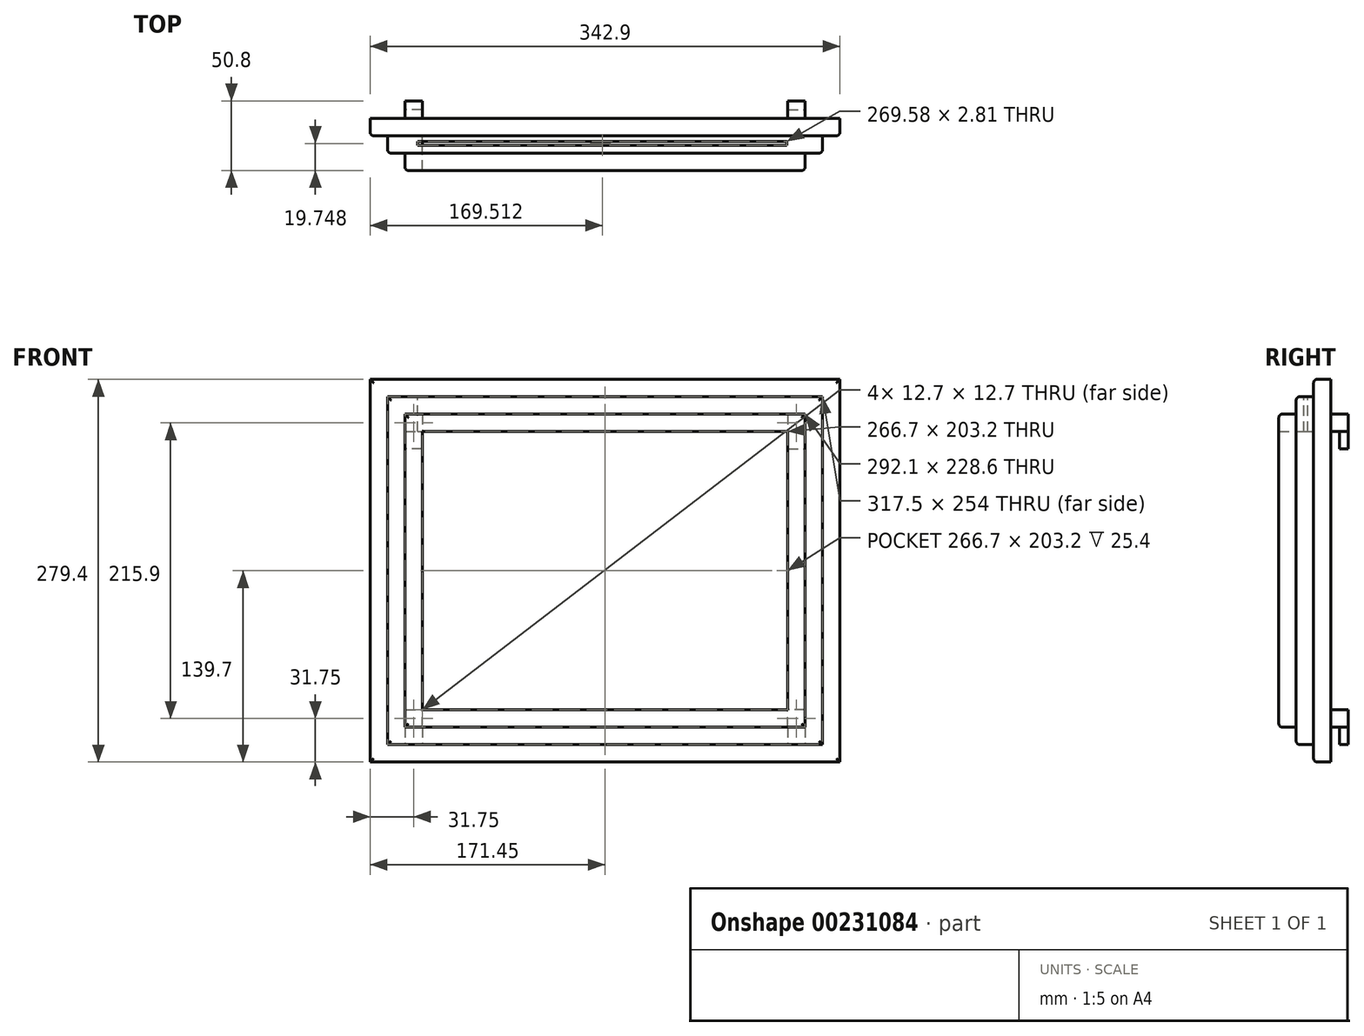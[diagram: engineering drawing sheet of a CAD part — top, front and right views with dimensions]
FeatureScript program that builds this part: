
annotation { "Feature Type Name" : "Feature", "Feature Type Description" : "" }
export const myFeature = defineFeature(function(context is Context, id is Id, definition is map)
    precondition{}
    {
        {
            var Q0;
            Q0=qCreatedBy(makeId("Front.planeOp"),FACE);
            var sketch = newSketch(context, id + "F0", { "sketchPlane" : qUnion([Q0])});
            skLineSegment(sketch, "E0.bottom", {"start": v(171.45, -139.7) * mm, "end": v(-171.45, -139.7) * mm});
            skLineSegment(sketch, "E0.top", {"start": v(171.45, 139.7) * mm, "end": v(-171.45, 139.7) * mm});
            skLineSegment(sketch, "E0.left", {"start": v(171.45, -139.7) * mm, "end": v(171.45, 139.7) * mm});
            skLineSegment(sketch, "E0.right", {"start": v(-171.45, -139.7) * mm, "end": v(-171.45, 139.7) * mm});
            skPoint(sketch, "E0.middle", {"position": v(0, 0) * mm});
            skSolve(sketch);
        }
        {
            var Q0;
            Q0 = qSketchRegion(id + "F0", true);
            extrude(context, id + "F1", {"entities" : qUnion([Q0]), "depth" : 12.7 * mm});
        }
        {
            var Q0;
            Q0=makeQuery(id+"F1.opExtrude","CAP_FACE",FACE,{"disambiguationData":[OSD([sQuery(id+"F0.wireOp",EDGE,"E0.bottom"),sQuery(id+"F0.wireOp",EDGE,"E0.top"),sQuery(id+"F0.wireOp",EDGE,"E0.left"),sQuery(id+"F0.wireOp",EDGE,"E0.right")])],"isStart":false});
            var sketch = newSketch(context, id + "F2", { "sketchPlane" : qUnion([Q0])});
            skLineSegment(sketch, "E1.bottom", {"start": v(158.75, 127) * mm, "end": v(-158.75, 127) * mm});
            skLineSegment(sketch, "E1.top", {"start": v(158.75, -127) * mm, "end": v(-158.75, -127) * mm});
            skLineSegment(sketch, "E1.left", {"start": v(158.75, 127) * mm, "end": v(158.75, -127) * mm});
            skLineSegment(sketch, "E1.right", {"start": v(-158.75, 127) * mm, "end": v(-158.75, -127) * mm});
            skPoint(sketch, "E1.middle", {"position": v(0, 0) * mm});
            skSolve(sketch);
        }
        {
            var Q0;
            Q0 = qSketchRegion(id + "F2", true);
            extrude(context, id + "F3", {"entities" : qUnion([Q0]), "operationType" : NewBodyOperationType.ADD, "depth" : 12.7 * mm});
        }
        {
            var Q0;
            Q0=makeQuery(id+"F3.opExtrude","CAP_FACE",FACE,{"disambiguationData":[OSD([sQuery(id+"F2.wireOp",EDGE,"E1.bottom"),sQuery(id+"F2.wireOp",EDGE,"E1.top"),sQuery(id+"F2.wireOp",EDGE,"E1.left"),sQuery(id+"F2.wireOp",EDGE,"E1.right")])],"isStart":false});
            var sketch = newSketch(context, id + "F4", { "sketchPlane" : qUnion([Q0])});
            skLineSegment(sketch, "E2.bottom", {"start": v(146.05, 114.3) * mm, "end": v(-146.05, 114.3) * mm});
            skLineSegment(sketch, "E2.top", {"start": v(146.05, -114.3) * mm, "end": v(-146.05, -114.3) * mm});
            skLineSegment(sketch, "E2.left", {"start": v(146.05, 114.3) * mm, "end": v(146.05, -114.3) * mm});
            skLineSegment(sketch, "E2.right", {"start": v(-146.05, 114.3) * mm, "end": v(-146.05, -114.3) * mm});
            skPoint(sketch, "E2.middle", {"position": v(0, 0) * mm});
            skSolve(sketch);
        }
        {
            var Q0;
            Q0 = qSketchRegion(id + "F4", true);
            extrude(context, id + "F5", {"entities" : qUnion([Q0]), "operationType" : NewBodyOperationType.ADD, "depth" : 12.7 * mm});
        }
        {
            var Q0;
            Q0=makeQuery(id+"F5.opExtrude","CAP_FACE",FACE,{"disambiguationData":[OSD([sQuery(id+"F4.wireOp",EDGE,"E2.bottom"),sQuery(id+"F4.wireOp",EDGE,"E2.top"),sQuery(id+"F4.wireOp",EDGE,"E2.left"),sQuery(id+"F4.wireOp",EDGE,"E2.right")])],"isStart":false});
            shell(context, id + "F6", {"entities" : qUnion([Q0]), "thickness" : 12.7 * mm});
        }
        {
            var Q0;
            Q0=makeQuery(id+"F3.opExtrude","SWEPT_FACE",FACE,{"disambiguationData":[OSD([sQuery(id+"F2.wireOp",EDGE,"E1.bottom")])]});
            var sketch = newSketch(context, id + "F7", { "sketchPlane" : qUnion([Q0])});
            skLineSegment(sketch, "E3.bottom", {"start": v(-139.7, -18.74) * mm, "end": v(139.7, -18.74) * mm});
            skLineSegment(sketch, "E3.top", {"start": v(-139.7, -21.91) * mm, "end": v(139.7, -21.91) * mm});
            skLineSegment(sketch, "E3.left", {"start": v(-139.7, -18.74) * mm, "end": v(-139.7, -21.91) * mm});
            skLineSegment(sketch, "E3.right", {"start": v(139.7, -18.74) * mm, "end": v(139.7, -21.91) * mm});
            skSolve(sketch);
        }
        {
            var Q0;
            Q0 = qSketchRegion(id + "F7", true);
            extrude(context, id + "F8", {"entities" : qUnion([Q0]), "operationType" : NewBodyOperationType.REMOVE, "oppositeDirection" : true, "depth" : 25.4 * mm});
        }
        {
            var Q0;
            Q0=makeQuery(id+"F5.opExtrude","CAP_EDGE",EDGE,{"disambiguationData":[OSD([sQuery(id+"F4.wireOp",EDGE,"E2.bottom")])],"isStart":false});
            var Q1;
            Q1=makeQuery(id+"F5.opExtrude","CAP_EDGE",EDGE,{"disambiguationData":[OSD([sQuery(id+"F4.wireOp",EDGE,"E2.left")])],"isStart":false});
            var Q2;
            Q2=makeQuery(id+"F3.opExtrude","CAP_EDGE",EDGE,{"disambiguationData":[OSD([sQuery(id+"F2.wireOp",EDGE,"E1.left")])],"isStart":false});
            var Q3;
            Q3=makeQuery(id+"F3.opExtrude","CAP_EDGE",EDGE,{"disambiguationData":[OSD([sQuery(id+"F2.wireOp",EDGE,"E1.bottom")])],"isStart":false});
            var Q4;
            Q4=makeQuery(id+"F1.opExtrude","CAP_EDGE",EDGE,{"disambiguationData":[OSD([sQuery(id+"F0.wireOp",EDGE,"E0.top")])],"isStart":false});
            var Q5;
            Q5=makeQuery(id+"F1.opExtrude","CAP_EDGE",EDGE,{"disambiguationData":[OSD([sQuery(id+"F0.wireOp",EDGE,"E0.left")])],"isStart":false});
            var Q6;
            Q6=makeQuery(id+"F5.opExtrude","CAP_EDGE",EDGE,{"disambiguationData":[OSD([sQuery(id+"F4.wireOp",EDGE,"E2.top")])],"isStart":false});
            var Q7;
            Q7=makeQuery(id+"F3.opExtrude","CAP_EDGE",EDGE,{"disambiguationData":[OSD([sQuery(id+"F2.wireOp",EDGE,"E1.top")])],"isStart":false});
            var Q8;
            Q8=makeQuery(id+"F1.opExtrude","CAP_EDGE",EDGE,{"disambiguationData":[OSD([sQuery(id+"F0.wireOp",EDGE,"E0.bottom")])],"isStart":false});
            var Q9;
            Q9=makeQuery(id+"F1.opExtrude","CAP_EDGE",EDGE,{"disambiguationData":[OSD([sQuery(id+"F0.wireOp",EDGE,"E0.right")])],"isStart":false});
            var Q10;
            Q10=makeQuery(id+"F3.opExtrude","CAP_EDGE",EDGE,{"disambiguationData":[OSD([sQuery(id+"F2.wireOp",EDGE,"E1.right")])],"isStart":false});
            var Q11;
            Q11=makeQuery(id+"F5.opExtrude","CAP_EDGE",EDGE,{"disambiguationData":[OSD([sQuery(id+"F4.wireOp",EDGE,"E2.right")])],"isStart":false});
            fillet(context, id + "F9", {"entities" : qUnion([Q0, Q1, Q2, Q3, Q4, Q5, Q6, Q7, Q8, Q9, Q10, Q11]), "radius" : 2.54 * mm, "tangentPropagation" : true, "allowEdgeOverflow" : false});
        }
        {
            var Q0;
            Q0=makeQuery(id+"F1.opExtrude","CAP_FACE",FACE,{"disambiguationData":[OSD([sQuery(id+"F0.wireOp",EDGE,"E0.bottom"),sQuery(id+"F0.wireOp",EDGE,"E0.top"),sQuery(id+"F0.wireOp",EDGE,"E0.left"),sQuery(id+"F0.wireOp",EDGE,"E0.right")])],"isStart":true});
            var sketch = newSketch(context, id + "F10", { "sketchPlane" : qUnion([Q0])});
            skLineSegment(sketch, "E4.bottom", {"start": v(-146.05, 114.3) * mm, "end": v(-133.35, 114.3) * mm});
            skLineSegment(sketch, "E4.top", {"start": v(-146.05, 101.6) * mm, "end": v(-133.35, 101.6) * mm});
            skLineSegment(sketch, "E4.left", {"start": v(-146.05, 114.3) * mm, "end": v(-146.05, 101.6) * mm});
            skLineSegment(sketch, "E4.right", {"start": v(-133.35, 114.3) * mm, "end": v(-133.35, 101.6) * mm});
            skSolve(sketch);
        }
        {
            var Q0;
            Q0 = qSketchRegion(id + "F10", true);
            extrude(context, id + "F11", {"entities" : qUnion([Q0]), "operationType" : NewBodyOperationType.ADD, "depth" : 12.7 * mm});
        }
        {
            var Q0;
            Q0=makeQuery(id+"F1.opExtrude","SWEPT_BODY",BODY,{"disambiguationData":[OSD([sQuery(id+"F0.wireOp",EDGE,"E0.bottom"),sQuery(id+"F0.wireOp",EDGE,"E0.top"),sQuery(id+"F0.wireOp",EDGE,"E0.left"),sQuery(id+"F0.wireOp",EDGE,"E0.right")])]});
            var Q1;
            Q1=qCreatedBy(makeId("Right.planeOp"),FACE);
            mirror(context, id + "F12", {"operationType" : NewBodyOperationType.ADD, "entities" : qUnion([Q0]), "mirrorPlane" : qUnion([Q1])});
        }
        {
            var Q0;
            Q0=makeQuery(id+"F1.opExtrude","SWEPT_BODY",BODY,{"disambiguationData":[OSD([sQuery(id+"F0.wireOp",EDGE,"E0.bottom"),sQuery(id+"F0.wireOp",EDGE,"E0.top"),sQuery(id+"F0.wireOp",EDGE,"E0.left"),sQuery(id+"F0.wireOp",EDGE,"E0.right")])]});
            var Q1;
            Q1=qCreatedBy(makeId("Top.planeOp"),FACE);
            mirror(context, id + "F13", {"operationType" : NewBodyOperationType.ADD, "entities" : qUnion([Q0]), "mirrorPlane" : qUnion([Q1])});
        }
        {
            var Q0;
            Q0=makeQuery(id+"F11.opExtrude","SWEPT_FACE",FACE,{"disambiguationData":[OSD([sQuery(id+"F10.wireOp",EDGE,"E4.left")])]});
            var sketch = newSketch(context, id + "F14", { "sketchPlane" : qUnion([Q0])});
            skPoint(sketch, "E5.oppositeSnap0", {"position": v(6.35, 101.6) * mm});
            skLineSegment(sketch, "E5.bottom", {"start": v(12.7, 101.6) * mm, "end": v(6.35, 101.6) * mm});
            skLineSegment(sketch, "E5.top", {"start": v(12.7, 88.9) * mm, "end": v(6.35, 88.9) * mm});
            skLineSegment(sketch, "E5.left", {"start": v(12.7, 101.6) * mm, "end": v(12.7, 88.9) * mm});
            skLineSegment(sketch, "E5.right", {"start": v(6.35, 101.6) * mm, "end": v(6.35, 88.9) * mm});
            skSolve(sketch);
        }
        {
            var Q0;
            Q0 = qSketchRegion(id + "F14", true);
            extrude(context, id + "F15", {"entities" : qUnion([Q0]), "oppositeDirection" : true, "depth" : 12.7 * mm});
        }
        {
            var Q0;
            Q0=makeQuery(id+"F15.opExtrude","SWEPT_BODY",BODY,{"disambiguationData":[OSD([sQuery(id+"F14.wireOp",EDGE,"E5.bottom"),sQuery(id+"F14.wireOp",EDGE,"E5.top"),sQuery(id+"F14.wireOp",EDGE,"E5.left"),sQuery(id+"F14.wireOp",EDGE,"E5.right")])]});
            var Q1;
            Q1=qCreatedBy(makeId("Right.planeOp"),FACE);
            mirror(context, id + "F16", {"entities" : qUnion([Q0]), "mirrorPlane" : qUnion([Q1])});
        }
        {
            var Q0;
            Q0=makeQuery(id+"F13.opPattern","COPY",FACE,{"derivedFrom":makeQuery(id+"F11.opExtrude","SWEPT_FACE",FACE,{"disambiguationData":[OSD([sQuery(id+"F10.wireOp",EDGE,"E4.left")])]}),"instanceName":"1"});
            var sketch = newSketch(context, id + "F17", { "sketchPlane" : qUnion([Q0])});
            skLineSegment(sketch, "E6.bottom", {"start": v(6.35, -114.3) * mm, "end": v(12.7, -114.3) * mm});
            skLineSegment(sketch, "E6.top", {"start": v(6.35, -127) * mm, "end": v(12.7, -127) * mm});
            skLineSegment(sketch, "E6.left", {"start": v(6.35, -114.3) * mm, "end": v(6.35, -127) * mm});
            skLineSegment(sketch, "E6.right", {"start": v(12.7, -114.3) * mm, "end": v(12.7, -127) * mm});
            skSolve(sketch);
        }
        {
            var Q0;
            Q0 = qSketchRegion(id + "F17", true);
            extrude(context, id + "F18", {"entities" : qUnion([Q0]), "operationType" : NewBodyOperationType.ADD, "oppositeDirection" : true, "depth" : 12.7 * mm});
        }
        {
            var Q0;
            Q0=makeQuery(id+"F1.opExtrude","SWEPT_BODY",BODY,{"disambiguationData":[OSD([sQuery(id+"F0.wireOp",EDGE,"E0.bottom"),sQuery(id+"F0.wireOp",EDGE,"E0.top"),sQuery(id+"F0.wireOp",EDGE,"E0.left"),sQuery(id+"F0.wireOp",EDGE,"E0.right")])]});
            var Q1;
            Q1=qCreatedBy(makeId("Right.planeOp"),FACE);
            mirror(context, id + "F19", {"entities" : qUnion([Q0]), "mirrorPlane" : qUnion([Q1])});
        }
        {
            var Q0;
            Q0=makeQuery(id+"F13.boolean.opBoolean","MERGE",FACE,{"derivedFrom":[makeQuery(id+"F3.opExtrude","SWEPT_FACE",FACE,{"disambiguationData":[OSD([sQuery(id+"F2.wireOp",EDGE,"E1.bottom")])]}),makeQuery(id+"F13.opPattern","COPY",FACE,{"derivedFrom":makeQuery(id+"F3.opExtrude","SWEPT_FACE",FACE,{"disambiguationData":[OSD([sQuery(id+"F2.wireOp",EDGE,"E1.top")])]}),"instanceName":"1"})]});
            var sketch = newSketch(context, id + "F20", { "sketchPlane" : qUnion([Q0])});
            skLineSegment(sketch, "E7", {"start": v(-136.73, -16.95) * mm, "end": v(132.85, -16.95) * mm});
            skLineSegment(sketch, "E8", {"start": v(132.85, -16.95) * mm, "end": v(132.85, -19.76) * mm});
            skLineSegment(sketch, "E9", {"start": v(132.85, -19.76) * mm, "end": v(-136.73, -19.76) * mm});
            skLineSegment(sketch, "E10", {"start": v(-136.73, -19.76) * mm, "end": v(-136.73, -16.95) * mm});
            skSolve(sketch);
        }
        {
            var Q0;
            Q0 = qSketchRegion(id + "F20", true);
            extrude(context, id + "F21", {"entities" : qUnion([Q0]), "operationType" : NewBodyOperationType.REMOVE, "oppositeDirection" : true, "depth" : 25.4 * mm});
        }
    });
